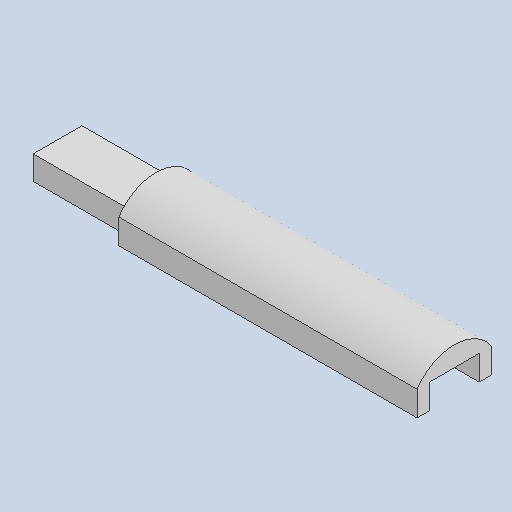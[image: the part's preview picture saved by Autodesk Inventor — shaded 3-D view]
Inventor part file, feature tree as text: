
AUTODESK INVENTOR PART (.ipt)
format: ipt  version: 2023 (Build 270158000, 158)  size: 108,032 bytes
history: native  units: in
note: dims shown in document units (in); Inventor stores cm internally (conversion verified against a paired STEP export)
features: other x3, sketch x3
ambient origin geometry x8: Origin, YZ Plane, XZ Plane, XY Plane, X Axis, Y Axis, Z Axis, Center Point
bodies: Solid1 (feature_tree)
feature tree (6):
  other  "Part_3_hand_extention.ipt"
  other  "Solid1::Part_3_hand_extention.ipt"
  other  "TaggingFeature1"
  sketch  "Sketch1"  dims[d0=0.3937in]
  sketch  "Sketch2"
  sketch  "Sketch3"
